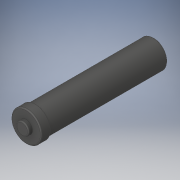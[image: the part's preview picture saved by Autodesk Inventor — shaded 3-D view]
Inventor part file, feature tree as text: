
AUTODESK INVENTOR PART (.ipt)
format: ipt  version: 2018.3 (Build 223284000, 284)  size: 140,800 bytes
history: native  units: in
note: dims shown in document units (in); Inventor stores cm internally (conversion verified against a paired STEP export)
features: other x1, fillet x1
ambient origin geometry x8: Origin, YZ Plane, XZ Plane, XY Plane, X Axis, Y Axis, Z Axis, Center Point
bodies: Solid1 (feature_tree)
feature tree (2):
  other  "Clippard Plastic Air Tank am-26491"
  fillet  "Fillet1"  [1 undecoded]
note: 1 required parameter value undecoded (feature->parameter linkage not recoverable at this tier; creation-order binding heuristic only, values carry confidence <= 0.55)
